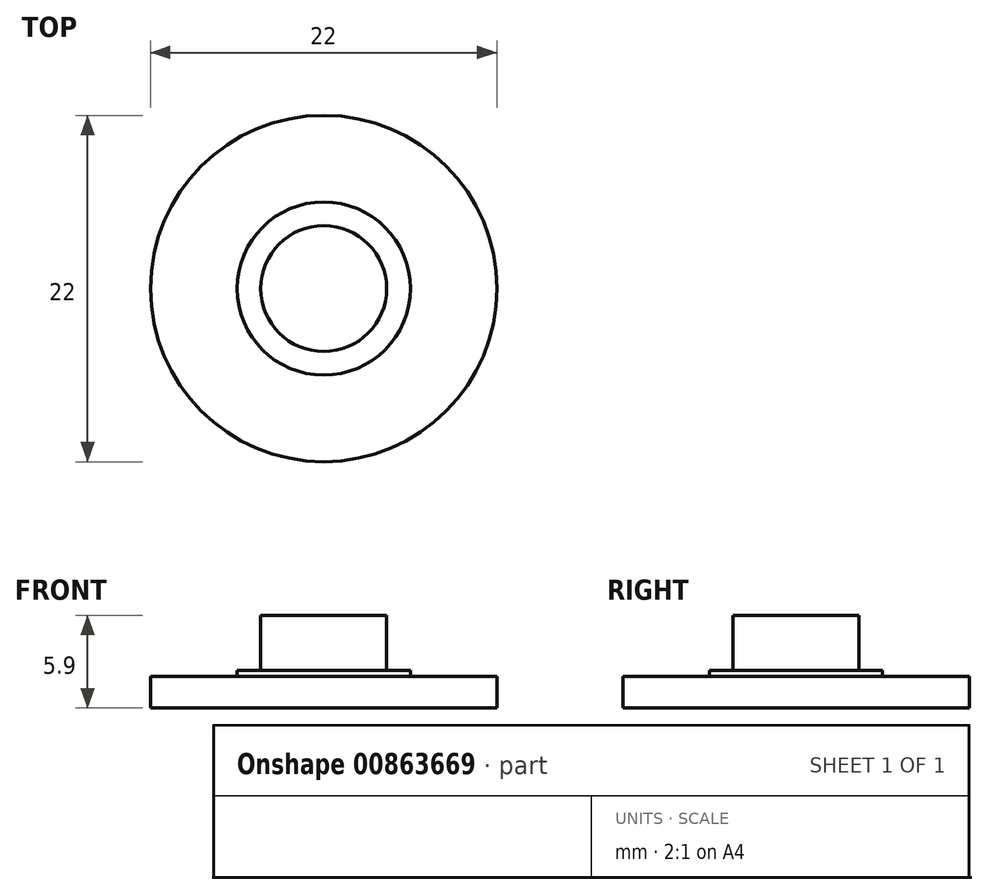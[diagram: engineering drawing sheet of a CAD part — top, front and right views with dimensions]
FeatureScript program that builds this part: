
annotation { "Feature Type Name" : "Feature", "Feature Type Description" : "" }
export const myFeature = defineFeature(function(context is Context, id is Id, definition is map)
    precondition{}
    {
        {
            assignVariable(context, id + "F0", {"name" : "depth", "anyValue" : 7});
        }
        {
            var Q0;
            Q0=qCreatedBy(makeId("Top.planeOp"),FACE);
            var sketch = newSketch(context, id + "F1", { "sketchPlane" : qUnion([Q0])});
            skCircle(sketch, "E0", {"center": v(0, 0) * mm, "radius": 11 * mm});
            skSolve(sketch);
        }
        {
            var Q0;
            Q0 = qSketchRegion(id + "F1", true);
            extrude(context, id + "F2", {"entities" : qUnion([Q0]), "depth" : 2 * mm, "offsetDistance" : 25 * mm});
        }
        {
            var Q0;
            Q0=makeQuery(id+"F2.opExtrude","CAP_FACE",FACE,{"disambiguationData":[OSD([sQuery(id+"F1.wireOp",EDGE,"E0")])],"isStart":false});
            var sketch = newSketch(context, id + "F3", { "sketchPlane" : qUnion([Q0])});
            skCircle(sketch, "E1", {"center": v(0, 0) * mm, "radius": 5.5 * mm});
            skSolve(sketch);
        }
        {
            var Q0;
            Q0 = qSketchRegion(id + "F3", true);
            extrude(context, id + "F4", {"entities" : qUnion([Q0]), "operationType" : NewBodyOperationType.ADD, "depth" : 0.4 * mm, "offsetDistance" : 25 * mm});
        }
        {
            var Q0;
            Q0=makeQuery(id+"F4.opExtrude","CAP_FACE",FACE,{"disambiguationData":[OSD([sQuery(id+"F3.wireOp",EDGE,"E1")])],"isStart":false});
            var sketch = newSketch(context, id + "F5", { "sketchPlane" : qUnion([Q0])});
            skCircle(sketch, "E2", {"center": v(0, 0) * mm, "radius": 4 * mm});
            skSolve(sketch);
        }
        {
            var Q0;
            Q0 = qSketchRegion(id + "F5", true);
            extrude(context, id + "F6", {"entities" : qUnion([Q0]), "operationType" : NewBodyOperationType.ADD, "depth" : (getVariable(context, 'depth') / 2) * mm, "offsetDistance" : 25 * mm});
        }
    });
